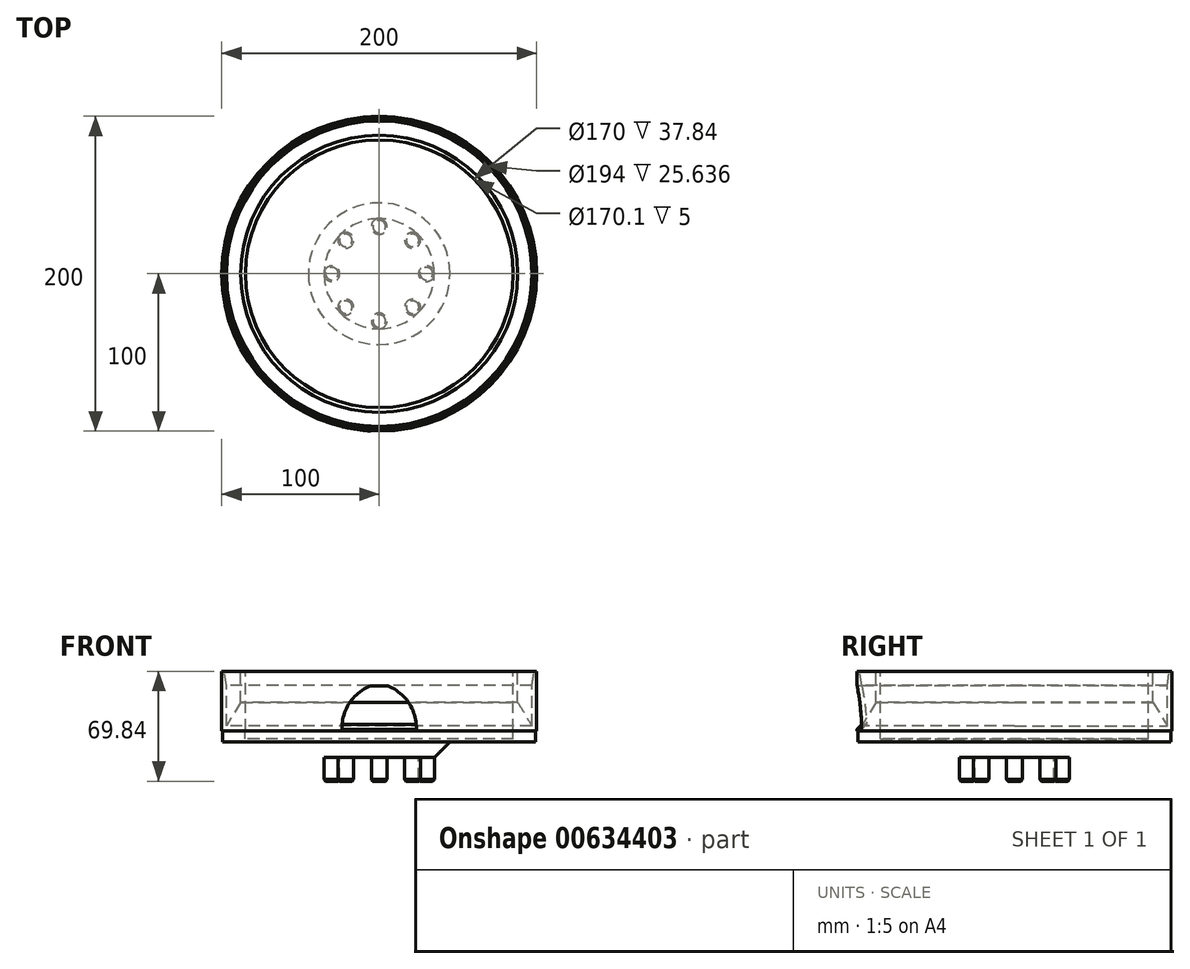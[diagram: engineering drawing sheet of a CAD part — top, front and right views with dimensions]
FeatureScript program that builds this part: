
annotation { "Feature Type Name" : "Feature", "Feature Type Description" : "" }
export const myFeature = defineFeature(function(context is Context, id is Id, definition is map)
    precondition{}
    {
        {
            var Q0;
            Q0=qCreatedBy(makeId("Top.planeOp"),FACE);
            var sketch = newSketch(context, id + "F0", { "sketchPlane" : qUnion([Q0])});
            skCircle(sketch, "E0", {"center": v(0, 0) * mm, "radius": 100 * mm});
            skCircle(sketch, "E1", {"center": v(0, 0) * mm, "radius": 85 * mm});
            skSolve(sketch);
        }
        {
            var Q0;
            Q0 = qSketchRegion(id + "F0", true);
            extrude(context, id + "F1", {"entities" : qUnion([Q0]), "oppositeDirection" : true, "depth" : 37.84 * mm, "offsetDistance" : 25 * mm});
        }
        {
            var Q0;
            Q0=makeQuery(id+"F1.opExtrude","CAP_FACE",FACE,{"disambiguationData":[OSD([sQuery(id+"F0.wireOp",EDGE,"E0"),sQuery(id+"F0.wireOp",EDGE,"E1")])],"isStart":true});
            shell(context, id + "F2", {"entities" : qUnion([Q0]), "thickness" : 3 * mm});
        }
        {
            var Q0;
            {var subQ0=sQuery(id+"F0.wireOp",EDGE,"E0");Q0=makeQuery(id+"F2.opShell","OFFSET_EDGE",EDGE,{"disambiguationData":[OSD([subQ0]),TDD([makeQuery(id+"F1.opExtrude","CAP_EDGE",EDGE,{"disambiguationData":[OSD([subQ0])],"isStart":true})])]});}
            chamfer(context, id + "F3", {"entities" : qUnion([Q0]), "chamferType" : ChamferType.TWO_OFFSETS, "width1" : 9 * mm, "oppositeDirection" : false, "width2" : 1.5 * mm, "tangentPropagation" : true});
        }
        {
            var Q0;
            {var subQ0=sQuery(id+"F0.wireOp",EDGE,"E1");Q0=makeQuery(id+"F2.opShell","OFFSET_EDGE",EDGE,{"disambiguationData":[OSD([subQ0]),TDD([makeQuery(id+"F1.opExtrude","CAP_EDGE",EDGE,{"disambiguationData":[OSD([subQ0])],"isStart":false})])]});}
            chamfer(context, id + "F4", {"entities" : qUnion([Q0]), "chamferType" : ChamferType.TWO_OFFSETS, "width1" : 15 * mm, "oppositeDirection" : false, "width2" : 9.12 * mm, "tangentPropagation" : true});
        }
        {
            var Q0;
            Q0=qCreatedBy(makeId("Front.planeOp"),FACE);
            cPlane(context, id + "F5", {"entities" : qUnion([Q0]), "cplaneType" : CPlaneType.OFFSET, "offset" : 100 * mm, "width" : 150 * mm, "height" : 150 * mm});
        }
        {
            var Q0;
            Q0=qCreatedBy(id+"F5.planeOp",FACE);
            var sketch = newSketch(context, id + "F6", { "sketchPlane" : qUnion([Q0])});
            skLineSegment(sketch, "E2.bottom", {"start": v(23.57, -33.84) * mm, "end": v(-23.57, -33.84) * mm});
            skLineSegment(sketch, "E2.top", {"start": v(5.49, -9.27) * mm, "end": v(-5.49, -9.27) * mm});
            skLineSegment(sketch, "E3", {"start": v(0, -33.84) * mm, "end": v(0, 8.43) * mm, "construction": true});
            skPoint(sketch, "E3.endSnap0", {"position": v(0, -9.27) * mm});
            skArc(sketch, "E4", {"start": v(23.57, -33.84) * mm, "mid": v(18.05, -18.96) * mm, "end": v(5.49, -9.27) * mm});
            skArc(sketch, "E5.MirrorCS", {"start": v(-23.57, -33.84) * mm, "mid": v(-18.05, -18.96) * mm, "end": v(-5.49, -9.27) * mm});
            skSolve(sketch);
        }
        {
            var Q0;
            Q0=makeQuery(id+"F6.imprint","IMPRINT",FACE,{"disambiguationData":[TD([[makeQuery(id+"F6.imprint","IMPRINT",EDGE,{"derivedFrom":sQuery(id+"F6.wireOp",EDGE,"E2.bottom")}),-1.0]])]});
            var Q1;
            Q1=makeQuery(id+"F2.opShell","OFFSET_FACE",FACE,{"disambiguationData":[OSD([sQuery(id+"F0.wireOp",EDGE,"E0")])]});
            extrude(context, id + "F7", {"entities" : qUnion([Q0]), "operationType" : NewBodyOperationType.REMOVE, "endBound" : BoundingType.UP_TO_SURFACE, "oppositeDirection" : true, "depth" : 25 * mm, "endBoundEntityFace" : qUnion([Q1]), "offsetDistance" : 25 * mm});
        }
        {
            var Q0;
            Q0=makeQuery(id+"F7.boolean.opBoolean","INTERSECT",EDGE,{"derivedFrom":[makeQuery(id+"F1.opExtrude","SWEPT_FACE",FACE,{"disambiguationData":[OSD([sQuery(id+"F0.wireOp",EDGE,"E0")])]}),makeQuery(id+"F7.opExtrude","SWEPT_FACE",FACE,{"disambiguationData":[OSD([sQuery(id+"F6.wireOp",EDGE,"E2.bottom")])]})]});
            chamfer(context, id + "F8", {"entities" : qUnion([Q0]), "width" : 3 * mm, "tangentPropagation" : true});
        }
        {
            var Q0;
            Q0=makeQuery(id+"F1.opExtrude","CAP_FACE",FACE,{"disambiguationData":[OSD([sQuery(id+"F0.wireOp",EDGE,"E0"),sQuery(id+"F0.wireOp",EDGE,"E1")])],"isStart":false});
            var sketch = newSketch(context, id + "F9", { "sketchPlane" : qUnion([Q0])});
            skCircle(sketch, "E6", {"center": v(0, 0) * mm, "radius": 99.36 * mm});
            skSolve(sketch);
        }
        {
            var Q0;
            Q0 = qSketchRegion(id + "F9", true);
            var Q1;
            Q1=sQuery(id+"F9.wireOp",EDGE,"E6");
            extrude(context, id + "F10", {"entities" : qUnion([Q0]), "operationType" : NewBodyOperationType.ADD, "surfaceEntities" : qUnion([Q1]), "depth" : 7 * mm, "offsetDistance" : 25 * mm});
        }
        {
            var Q0;
            Q0=makeQuery(id+"F10.opExtrude","CAP_FACE",FACE,{"disambiguationData":[OSD([sQuery(id+"F9.wireOp",EDGE,"E6")])],"isStart":true});
            var sketch = newSketch(context, id + "F11", { "sketchPlane" : qUnion([Q0])});
            skCircle(sketch, "E7", {"center": v(0, 0) * mm, "radius": 85.05 * mm});
            skSolve(sketch);
        }
        {
            var Q0;
            Q0 = qSketchRegion(id + "F11", true);
            extrude(context, id + "F12", {"entities" : qUnion([Q0]), "operationType" : NewBodyOperationType.REMOVE, "oppositeDirection" : true, "depth" : 5 * mm, "offsetDistance" : 25 * mm});
        }
        {
            var Q0;
            Q0=makeQuery(id+"F10.opExtrude","CAP_FACE",FACE,{"disambiguationData":[OSD([sQuery(id+"F9.wireOp",EDGE,"E6")])],"isStart":false});
            var sketch = newSketch(context, id + "F13", { "sketchPlane" : qUnion([Q0])});
            skCircle(sketch, "E8", {"center": v(0, 0) * mm, "radius": 45 * mm});
            skSolve(sketch);
        }
        {
            var Q0;
            Q0 = qSketchRegion(id + "F13", true);
            extrude(context, id + "F14", {"entities" : qUnion([Q0]), "operationType" : NewBodyOperationType.ADD, "depth" : 10 * mm, "offsetDistance" : 25 * mm});
        }
        {
            var Q0;
            Q0=makeQuery(id+"F14.opExtrude","CAP_EDGE",EDGE,{"disambiguationData":[OSD([sQuery(id+"F13.wireOp",EDGE,"E8")])],"isStart":false});
            chamfer(context, id + "F15", {"entities" : qUnion([Q0]), "width" : 10 * mm, "tangentPropagation" : true});
        }
        {
            var Q0;
            Q0=makeQuery(id+"F14.opExtrude","CAP_FACE",FACE,{"disambiguationData":[OSD([sQuery(id+"F13.wireOp",EDGE,"E8")])],"isStart":false});
            var sketch = newSketch(context, id + "F16", { "sketchPlane" : qUnion([Q0])});
            skCircle(sketch, "E9", {"center": v(0, 30) * mm, "radius": 5 * mm});
            skPoint(sketch, "E10.center", {"position": v(0, 0) * mm});
            skSolve(sketch);
        }
        {
            var Q0;
            Q0 = qSketchRegion(id + "F16", true);
            var Q1;
            Q1 = qConstructionFilter(qBodyType(qCreatedBy(id + "F16" ,EDGE), BodyType.WIRE), ConstructionObject.NO);
            extrude(context, id + "F17", {"entities" : qUnion([Q0]), "surfaceEntities" : qUnion([Q1]), "depth" : 15 * mm, "offsetDistance" : 25 * mm});
        }
        {
            var Q0;
            Q0=makeQuery(id+"F17.opExtrude","CAP_EDGE",EDGE,{"disambiguationData":[OSD([sQuery(id+"F16.wireOp",EDGE,"E9")])],"isStart":false});
            chamfer(context, id + "F18", {"entities" : qUnion([Q0]), "width" : 1 * mm, "tangentPropagation" : true});
        }
        {
            var Q0;
            Q0=qCreatedBy(makeId("Right.planeOp"),FACE);
            var sketch = newSketch(context, id + "F19", { "sketchPlane" : qUnion([Q0])});
            skLineSegment(sketch, "E11", {"start": v(0, 0) * mm, "end": v(0, -118.01) * mm, "construction": true});
            skSolve(sketch);
        }
        {
            var Q0;
            Q0=makeQuery(id+"F17.opExtrude","SWEPT_BODY",BODY,{"disambiguationData":[OSD([sQuery(id+"F16.wireOp",EDGE,"E9")])]});
            var Q1;
            Q1=sQuery(id+"F19.wireOp",EDGE,"E11");
            circularPattern(context, id + "F20", {"operationType" : NewBodyOperationType.ADD, "entities" : qUnion([Q0]), "axis" : qUnion([Q1]), "angle" : 360 * degree, "instanceCount" : 8, "equalSpace" : true});
        }
    });
